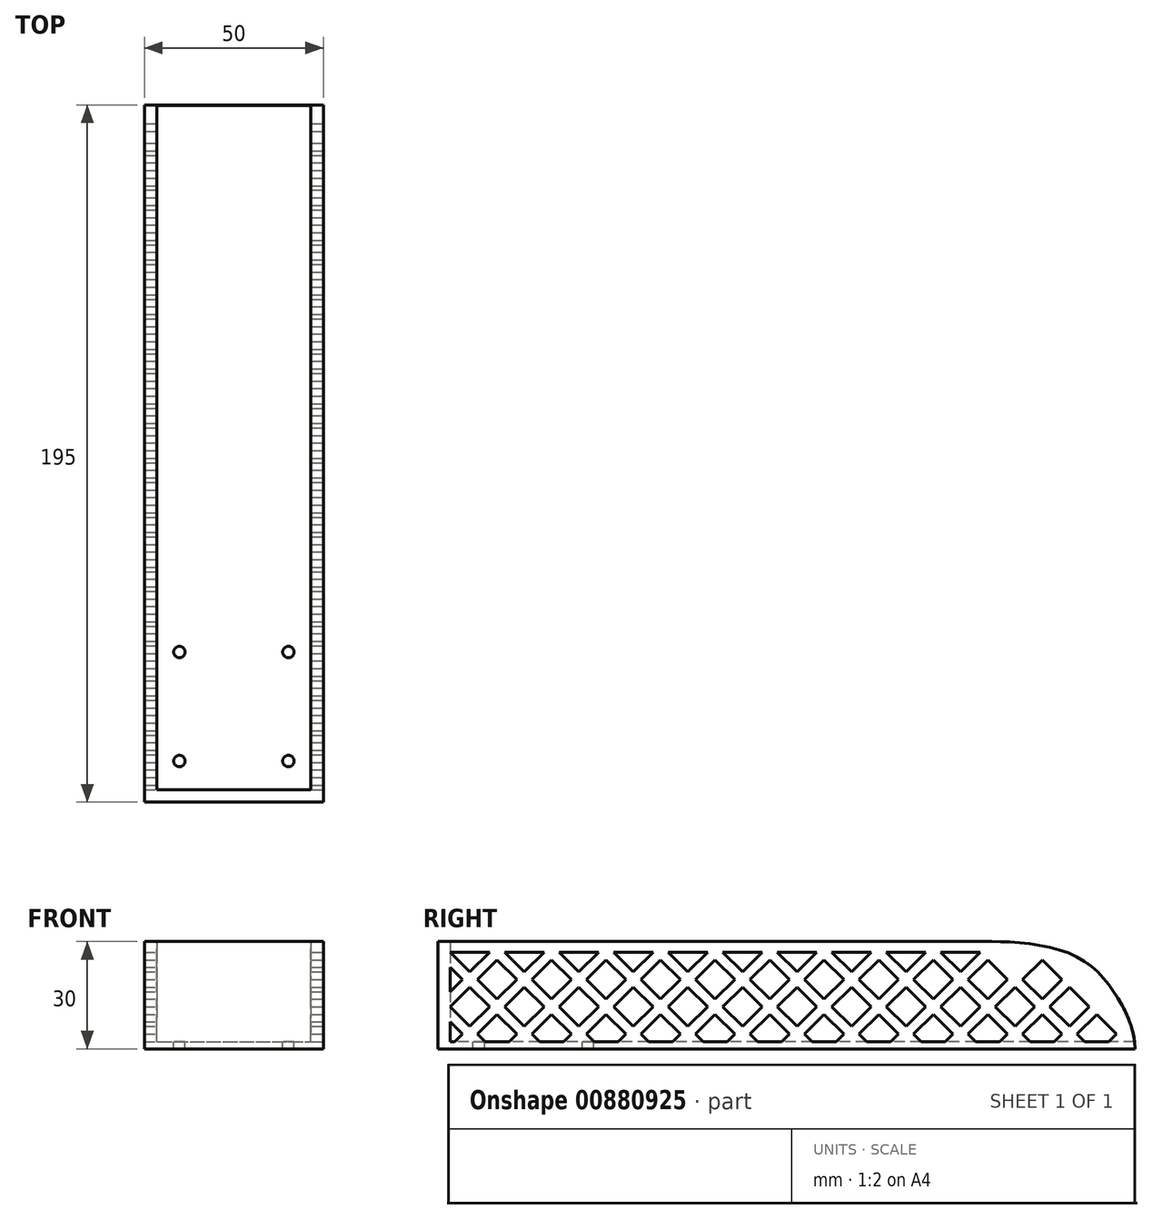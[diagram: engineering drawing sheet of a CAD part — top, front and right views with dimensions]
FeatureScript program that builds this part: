
annotation { "Feature Type Name" : "Feature", "Feature Type Description" : "" }
export const myFeature = defineFeature(function(context is Context, id is Id, definition is map)
    precondition{}
    {
        {
            var Q0;
            Q0=qCreatedBy(makeId("Top.planeOp"),FACE);
            var sketch = newSketch(context, id + "F0", { "sketchPlane" : qUnion([Q0])});
            skLineSegment(sketch, "E0.bottom", {"start": v(0, 0) * mm, "end": v(50, 0) * mm});
            skLineSegment(sketch, "E0.top", {"start": v(0, 195) * mm, "end": v(50, 195) * mm});
            skLineSegment(sketch, "E0.left", {"start": v(0, 0) * mm, "end": v(0, 195) * mm});
            skLineSegment(sketch, "E0.right", {"start": v(50, 0) * mm, "end": v(50, 195) * mm});
            skSolve(sketch);
        }
        {
            var Q0;
            Q0=makeQuery(id+"F0.imprint","IMPRINT",FACE,{"disambiguationData":[TD([[makeQuery(id+"F0.imprint","IMPRINT",EDGE,{"derivedFrom":sQuery(id+"F0.wireOp",EDGE,"E0.bottom")}),1.0]])]});
            extrude(context, id + "F1", {"entities" : qUnion([Q0]), "depth" : 2 * mm, "offsetDistance" : 25 * mm});
        }
        {
            var Q0;
            Q0=makeQuery(id+"F1.opExtrude","CAP_FACE",FACE,{"disambiguationData":[OSD([sQuery(id+"F0.wireOp",EDGE,"E0.bottom"),sQuery(id+"F0.wireOp",EDGE,"E0.top"),sQuery(id+"F0.wireOp",EDGE,"E0.left"),sQuery(id+"F0.wireOp",EDGE,"E0.right")])],"isStart":false});
            var sketch = newSketch(context, id + "F2", { "sketchPlane" : qUnion([Q0])});
            skLineSegment(sketch, "E1.0.0", {"start": v(50, 195) * mm, "end": v(0, 195) * mm});
            skLineSegment(sketch, "E1.0.1", {"start": v(0, 195) * mm, "end": v(0, 0) * mm});
            skLineSegment(sketch, "E1.0.2", {"start": v(0, 0) * mm, "end": v(50, 0) * mm});
            skLineSegment(sketch, "E1.0.3", {"start": v(50, 0) * mm, "end": v(50, 195) * mm});
            skLineSegment(sketch, "E2", {"start": v(3.5, 195) * mm, "end": v(3.5, 3.5) * mm});
            skLineSegment(sketch, "E3", {"start": v(3.5, 3.5) * mm, "end": v(46.5, 3.5) * mm});
            skLineSegment(sketch, "E4", {"start": v(46.5, 3.5) * mm, "end": v(46.5, 195) * mm});
            skLineSegment(sketch, "E5", {"start": v(0, 195) * mm, "end": v(3.5, 195) * mm});
            skLineSegment(sketch, "E6", {"start": v(46.5, 195) * mm, "end": v(50, 195) * mm});
            skSolve(sketch);
        }
        {
            var Q0;
            {var subQ0=sQuery(id+"F2.wireOp",EDGE,"E1.0.1");Q0=makeQuery(id+"F2.imprint","IMPRINT",FACE,{"disambiguationData":[TD([[makeQuery(id+"F2.imprint","IMPRINT",EDGE,{"derivedFrom":subQ0}),-1.0]])]});}
            extrude(context, id + "F3", {"entities" : qUnion([Q0]), "operationType" : NewBodyOperationType.ADD, "depth" : 28 * mm, "offsetDistance" : 25 * mm});
        }
        {
            var Q0;
            Q0=makeQuery(id+"F3.boolean.opBoolean","MERGE",FACE,{"derivedFrom":[makeQuery(id+"F1.opExtrude","SWEPT_FACE",FACE,{"disambiguationData":[OSD([sQuery(id+"F0.wireOp",EDGE,"E0.right")])]}),makeQuery(id+"F3.opExtrude","SWEPT_FACE",FACE,{"disambiguationData":[OSD([sQuery(id+"F2.wireOp",EDGE,"E1.0.3")])]})]});
            var sketch = newSketch(context, id + "F4", { "sketchPlane" : qUnion([Q0])});
            skLineSegment(sketch, "E7.0.0", {"start": v(0, 0) * mm, "end": v(195, 0) * mm});
            skLineSegment(sketch, "E7.0.1", {"start": v(195, 0) * mm, "end": v(195, 30) * mm});
            skLineSegment(sketch, "E7.0.2", {"start": v(195, 30) * mm, "end": v(0, 30) * mm});
            skLineSegment(sketch, "E7.0.3", {"start": v(0, 30) * mm, "end": v(0, 0) * mm});
            skFitSpline(sketch, "E8", {"points": [v(195, 0) * mm, v(190.35, 13.95) * mm, v(177.8, 26.18) * mm, v(155, 30) * mm], "startDerivative": vector(0, 46.4) * mm, "endDerivative": vector(-53.38, 0) * mm});
            skSolve(sketch);
        }
        {
            var Q0;
            {var subQ0=sQuery(id+"F4.wireOp",EDGE,"E7.0.1");Q0=makeQuery(id+"F4.imprint","IMPRINT",FACE,{"disambiguationData":[TD([[makeQuery(id+"F4.imprint","IMPRINT",EDGE,{"derivedFrom":subQ0}),-1.0]])]});}
            extrude(context, id + "F5", {"entities" : qUnion([Q0]), "operationType" : NewBodyOperationType.REMOVE, "endBound" : BoundingType.THROUGH_ALL, "oppositeDirection" : true, "depth" : 25 * mm, "offsetDistance" : 25 * mm});
        }
        {
            var Q0;
            Q0=makeQuery(id+"F3.boolean.opBoolean","MERGE",FACE,{"derivedFrom":[makeQuery(id+"F1.opExtrude","SWEPT_FACE",FACE,{"disambiguationData":[OSD([sQuery(id+"F0.wireOp",EDGE,"E0.right")])]}),makeQuery(id+"F3.opExtrude","SWEPT_FACE",FACE,{"disambiguationData":[OSD([sQuery(id+"F2.wireOp",EDGE,"E1.0.3")])]})]});
            var sketch = newSketch(context, id + "F6", { "sketchPlane" : qUnion([Q0])});
            skLineSegment(sketch, "E9.0.0", {"start": v(0, 0) * mm, "end": v(195, 0) * mm});
            skFitSpline(sketch, "E9.0.1", {"points": [v(195, 0) * mm, v(195, 4.62) * mm, v(190.89, 14.7) * mm, v(179.29, 28.71) * mm, v(161.67, 30) * mm, v(155, 30) * mm]});
            skLineSegment(sketch, "E9.0.2", {"start": v(155, 30) * mm, "end": v(0, 30) * mm});
            skLineSegment(sketch, "E9.0.3", {"start": v(0, 30) * mm, "end": v(0, 0) * mm});
            skLineSegment(sketch, "E10.0.1", {"start": v(3.5, 2) * mm, "end": v(3.5, 30) * mm});
            skLineSegment(sketch, "E10.0.3", {"start": v(3.5, 30) * mm, "end": v(3.5, 2) * mm});
            skLineSegment(sketch, "E11.0.0", {"start": v(3.5, 2) * mm, "end": v(194.88, 2) * mm});
            skLineSegment(sketch, "E11.0.2", {"start": v(194.88, 2) * mm, "end": v(3.5, 2) * mm});
            skLineSegment(sketch, "E12.0", {"start": v(155, 27) * mm, "end": v(0, 27) * mm});
            skFitSpline(sketch, "E12.1", {"points": [v(192, 0) * mm, v(192, 0.79) * mm, v(191.86, 2.41) * mm, v(191.25, 4.98) * mm, v(190.28, 7.63) * mm, v(189.2, 9.87) * mm, v(188.22, 11.66) * mm, v(187.16, 13.45) * mm, v(185.75, 15.6) * mm, v(183.86, 17.98) * mm, v(181.74, 20.11) * mm, v(179.74, 21.66) * mm, v(177.97, 22.74) * mm, v(176.56, 23.47) * mm, v(175.02, 24.12) * mm, v(173.36, 24.7) * mm, v(171.6, 25.2) * mm, v(169.17, 25.78) * mm, v(165.98, 26.33) * mm, v(160.83, 26.89) * mm, v(157.16, 27) * mm, v(155, 27) * mm]});
            skLineSegment(sketch, "E13", {"start": v(3.5, 27) * mm, "end": v(9, 21.5) * mm});
            skLineSegment(sketch, "E14", {"start": v(9, 21.5) * mm, "end": v(14.5, 27) * mm});
            skLineSegment(sketch, "E15", {"start": v(3.5, 22.76) * mm, "end": v(6.88, 19.38) * mm});
            skLineSegment(sketch, "E16", {"start": v(6.88, 19.38) * mm, "end": v(3.5, 16) * mm});
            skLineSegment(sketch, "E17", {"start": v(9, 17.26) * mm, "end": v(3.5, 11.76) * mm});
            skLineSegment(sketch, "E18", {"start": v(3.5, 11.76) * mm, "end": v(9, 6.26) * mm});
            skLineSegment(sketch, "E19", {"start": v(9, 6.26) * mm, "end": v(14.5, 11.76) * mm});
            skLineSegment(sketch, "E20", {"start": v(14.5, 11.76) * mm, "end": v(9, 17.26) * mm});
            skLineSegment(sketch, "E21", {"start": v(6.88, 19.38) * mm, "end": v(9, 21.5) * mm, "construction": true});
            skLineSegment(sketch, "E22", {"start": v(3.5, 11.76) * mm, "end": v(14.5, 11.76) * mm, "construction": true});
            skLineSegment(sketch, "E23.MirrorCS", {"start": v(4.74, 2) * mm, "end": v(6.88, 4.14) * mm});
            skLineSegment(sketch, "E24.MirrorCS", {"start": v(6.88, 4.14) * mm, "end": v(3.5, 7.51) * mm});
            skPoint(sketch, "E25.orphan", {"position": v(3.5, 0.76) * mm});
            skLineSegment(sketch, "E26", {"start": v(9, 21.5) * mm, "end": v(9, 17.26) * mm, "construction": true});
            skLineSegment(sketch, "E27", {"start": v(11.12, 19.38) * mm, "end": v(16.62, 24.88) * mm});
            skLineSegment(sketch, "E28", {"start": v(11.12, 19.38) * mm, "end": v(16.62, 13.88) * mm});
            skLineSegment(sketch, "E29", {"start": v(16.62, 13.88) * mm, "end": v(22.12, 19.38) * mm});
            skLineSegment(sketch, "E30", {"start": v(22.12, 19.38) * mm, "end": v(16.62, 24.88) * mm});
            skLineSegment(sketch, "E31", {"start": v(6.88, 19.38) * mm, "end": v(11.12, 19.38) * mm, "construction": true});
            skLineSegment(sketch, "E32.MirrorCS", {"start": v(11.12, 4.14) * mm, "end": v(13.26, 2) * mm});
            skLineSegment(sketch, "E33.MirrorCS", {"start": v(22.12, 4.14) * mm, "end": v(19.99, 2) * mm});
            skLineSegment(sketch, "E34.MirrorCS", {"start": v(16.62, 9.64) * mm, "end": v(22.12, 4.14) * mm});
            skLineSegment(sketch, "E35.MirrorCS", {"start": v(11.12, 4.14) * mm, "end": v(16.62, 9.64) * mm});
            skPoint(sketch, "E36.orphan", {"position": v(16.62, -1.36) * mm});
            skLineSegment(sketch, "E37.1.0.0", {"start": v(18.74, 27) * mm, "end": v(24.24, 21.5) * mm});
            skLineSegment(sketch, "E37.1.0.1", {"start": v(24.24, 21.5) * mm, "end": v(29.74, 27) * mm});
            skLineSegment(sketch, "E37.1.0.2", {"start": v(26.36, 19.38) * mm, "end": v(31.86, 24.88) * mm});
            skLineSegment(sketch, "E37.1.0.3", {"start": v(37.36, 19.38) * mm, "end": v(31.86, 24.88) * mm});
            skLineSegment(sketch, "E37.1.0.4", {"start": v(31.86, 13.88) * mm, "end": v(37.36, 19.38) * mm});
            skLineSegment(sketch, "E37.1.0.5", {"start": v(26.36, 19.38) * mm, "end": v(31.86, 13.88) * mm});
            skLineSegment(sketch, "E37.1.0.6", {"start": v(29.74, 11.76) * mm, "end": v(24.24, 17.26) * mm});
            skLineSegment(sketch, "E37.1.0.7", {"start": v(24.24, 17.26) * mm, "end": v(18.74, 11.76) * mm});
            skLineSegment(sketch, "E37.1.0.8", {"start": v(18.74, 11.76) * mm, "end": v(24.24, 6.26) * mm});
            skLineSegment(sketch, "E37.1.0.9", {"start": v(24.24, 6.26) * mm, "end": v(29.74, 11.76) * mm});
            skLineSegment(sketch, "E37.1.0.10", {"start": v(26.36, 4.14) * mm, "end": v(31.86, 9.64) * mm});
            skLineSegment(sketch, "E37.1.0.11", {"start": v(31.86, 9.64) * mm, "end": v(37.36, 4.14) * mm});
            skLineSegment(sketch, "E37.1.0.12", {"start": v(37.36, 4.14) * mm, "end": v(35.23, 2) * mm});
            skLineSegment(sketch, "E37.1.0.13", {"start": v(26.36, 4.14) * mm, "end": v(28.5, 2) * mm});
            skLineSegment(sketch, "E37.2.0.0", {"start": v(33.99, 27) * mm, "end": v(39.49, 21.5) * mm});
            skLineSegment(sketch, "E37.2.0.1", {"start": v(39.49, 21.5) * mm, "end": v(44.99, 27) * mm});
            skLineSegment(sketch, "E37.2.0.2", {"start": v(41.6, 19.38) * mm, "end": v(47.1, 24.88) * mm});
            skLineSegment(sketch, "E37.2.0.3", {"start": v(52.6, 19.38) * mm, "end": v(47.1, 24.88) * mm});
            skLineSegment(sketch, "E37.2.0.4", {"start": v(47.1, 13.88) * mm, "end": v(52.6, 19.38) * mm});
            skLineSegment(sketch, "E37.2.0.5", {"start": v(41.6, 19.38) * mm, "end": v(47.1, 13.88) * mm});
            skLineSegment(sketch, "E37.2.0.6", {"start": v(44.99, 11.76) * mm, "end": v(39.49, 17.26) * mm});
            skLineSegment(sketch, "E37.2.0.7", {"start": v(39.49, 17.26) * mm, "end": v(33.99, 11.76) * mm});
            skLineSegment(sketch, "E37.2.0.8", {"start": v(33.99, 11.76) * mm, "end": v(39.49, 6.26) * mm});
            skLineSegment(sketch, "E37.2.0.9", {"start": v(39.49, 6.26) * mm, "end": v(44.99, 11.76) * mm});
            skLineSegment(sketch, "E37.2.0.10", {"start": v(41.6, 4.14) * mm, "end": v(47.1, 9.64) * mm});
            skLineSegment(sketch, "E37.2.0.11", {"start": v(47.1, 9.64) * mm, "end": v(52.6, 4.14) * mm});
            skLineSegment(sketch, "E37.2.0.12", {"start": v(52.6, 4.14) * mm, "end": v(50.47, 2) * mm});
            skLineSegment(sketch, "E37.2.0.13", {"start": v(41.6, 4.14) * mm, "end": v(43.74, 2) * mm});
            skLineSegment(sketch, "E37.3.0.0", {"start": v(49.23, 27) * mm, "end": v(54.73, 21.5) * mm});
            skLineSegment(sketch, "E37.3.0.1", {"start": v(54.73, 21.5) * mm, "end": v(60.23, 27) * mm});
            skLineSegment(sketch, "E37.3.0.2", {"start": v(56.85, 19.38) * mm, "end": v(62.35, 24.88) * mm});
            skLineSegment(sketch, "E37.3.0.3", {"start": v(67.85, 19.38) * mm, "end": v(62.35, 24.88) * mm});
            skLineSegment(sketch, "E37.3.0.4", {"start": v(62.35, 13.88) * mm, "end": v(67.85, 19.38) * mm});
            skLineSegment(sketch, "E37.3.0.5", {"start": v(56.85, 19.38) * mm, "end": v(62.35, 13.88) * mm});
            skLineSegment(sketch, "E37.3.0.6", {"start": v(60.23, 11.76) * mm, "end": v(54.73, 17.26) * mm});
            skLineSegment(sketch, "E37.3.0.7", {"start": v(54.73, 17.26) * mm, "end": v(49.23, 11.76) * mm});
            skLineSegment(sketch, "E37.3.0.8", {"start": v(49.23, 11.76) * mm, "end": v(54.73, 6.26) * mm});
            skLineSegment(sketch, "E37.3.0.9", {"start": v(54.73, 6.26) * mm, "end": v(60.23, 11.76) * mm});
            skLineSegment(sketch, "E37.3.0.10", {"start": v(56.85, 4.14) * mm, "end": v(62.35, 9.64) * mm});
            skLineSegment(sketch, "E37.3.0.11", {"start": v(62.35, 9.64) * mm, "end": v(67.85, 4.14) * mm});
            skLineSegment(sketch, "E37.3.0.12", {"start": v(67.85, 4.14) * mm, "end": v(65.71, 2) * mm});
            skLineSegment(sketch, "E37.3.0.13", {"start": v(56.85, 4.14) * mm, "end": v(58.99, 2) * mm});
            skLineSegment(sketch, "E37.4.0.0", {"start": v(64.47, 27) * mm, "end": v(69.97, 21.5) * mm});
            skLineSegment(sketch, "E37.4.0.1", {"start": v(69.97, 21.5) * mm, "end": v(75.47, 27) * mm});
            skLineSegment(sketch, "E37.4.0.2", {"start": v(72.1, 19.38) * mm, "end": v(77.6, 24.88) * mm});
            skLineSegment(sketch, "E37.4.0.3", {"start": v(83.1, 19.38) * mm, "end": v(77.6, 24.88) * mm});
            skLineSegment(sketch, "E37.4.0.4", {"start": v(77.6, 13.88) * mm, "end": v(83.1, 19.38) * mm});
            skLineSegment(sketch, "E37.4.0.5", {"start": v(72.1, 19.38) * mm, "end": v(77.6, 13.88) * mm});
            skLineSegment(sketch, "E37.4.0.6", {"start": v(75.47, 11.76) * mm, "end": v(69.97, 17.26) * mm});
            skLineSegment(sketch, "E37.4.0.7", {"start": v(69.97, 17.26) * mm, "end": v(64.47, 11.76) * mm});
            skLineSegment(sketch, "E37.4.0.8", {"start": v(64.47, 11.76) * mm, "end": v(69.97, 6.26) * mm});
            skLineSegment(sketch, "E37.4.0.9", {"start": v(69.97, 6.26) * mm, "end": v(75.47, 11.76) * mm});
            skLineSegment(sketch, "E37.4.0.10", {"start": v(72.1, 4.14) * mm, "end": v(77.6, 9.64) * mm});
            skLineSegment(sketch, "E37.4.0.11", {"start": v(77.6, 9.64) * mm, "end": v(83.1, 4.14) * mm});
            skLineSegment(sketch, "E37.4.0.12", {"start": v(83.1, 4.14) * mm, "end": v(80.96, 2) * mm});
            skLineSegment(sketch, "E37.4.0.13", {"start": v(72.1, 4.14) * mm, "end": v(74.23, 2) * mm});
            skLineSegment(sketch, "E37.5.0.0", {"start": v(79.72, 27) * mm, "end": v(85.22, 21.5) * mm});
            skLineSegment(sketch, "E37.5.0.1", {"start": v(85.22, 21.5) * mm, "end": v(90.72, 27) * mm});
            skLineSegment(sketch, "E37.5.0.2", {"start": v(87.34, 19.38) * mm, "end": v(92.84, 24.88) * mm});
            skLineSegment(sketch, "E37.5.0.3", {"start": v(98.34, 19.38) * mm, "end": v(92.84, 24.88) * mm});
            skLineSegment(sketch, "E37.5.0.4", {"start": v(92.84, 13.88) * mm, "end": v(98.34, 19.38) * mm});
            skLineSegment(sketch, "E37.5.0.5", {"start": v(87.34, 19.38) * mm, "end": v(92.84, 13.88) * mm});
            skLineSegment(sketch, "E37.5.0.6", {"start": v(90.72, 11.76) * mm, "end": v(85.22, 17.26) * mm});
            skLineSegment(sketch, "E37.5.0.7", {"start": v(85.22, 17.26) * mm, "end": v(79.72, 11.76) * mm});
            skLineSegment(sketch, "E37.5.0.8", {"start": v(79.72, 11.76) * mm, "end": v(85.22, 6.26) * mm});
            skLineSegment(sketch, "E37.5.0.9", {"start": v(85.22, 6.26) * mm, "end": v(90.72, 11.76) * mm});
            skLineSegment(sketch, "E37.5.0.10", {"start": v(87.34, 4.14) * mm, "end": v(92.84, 9.64) * mm});
            skLineSegment(sketch, "E37.5.0.11", {"start": v(92.84, 9.64) * mm, "end": v(98.34, 4.14) * mm});
            skLineSegment(sketch, "E37.5.0.12", {"start": v(98.34, 4.14) * mm, "end": v(96.2, 2) * mm});
            skLineSegment(sketch, "E37.5.0.13", {"start": v(87.34, 4.14) * mm, "end": v(89.47, 2) * mm});
            skLineSegment(sketch, "E37.6.0.0", {"start": v(94.96, 27) * mm, "end": v(100.46, 21.5) * mm});
            skLineSegment(sketch, "E37.6.0.1", {"start": v(100.46, 21.5) * mm, "end": v(105.96, 27) * mm});
            skLineSegment(sketch, "E37.6.0.2", {"start": v(102.58, 19.38) * mm, "end": v(108.08, 24.88) * mm});
            skLineSegment(sketch, "E37.6.0.3", {"start": v(113.58, 19.38) * mm, "end": v(108.08, 24.88) * mm});
            skLineSegment(sketch, "E37.6.0.4", {"start": v(108.08, 13.88) * mm, "end": v(113.58, 19.38) * mm});
            skLineSegment(sketch, "E37.6.0.5", {"start": v(102.58, 19.38) * mm, "end": v(108.08, 13.88) * mm});
            skLineSegment(sketch, "E37.6.0.6", {"start": v(105.96, 11.76) * mm, "end": v(100.46, 17.26) * mm});
            skLineSegment(sketch, "E37.6.0.7", {"start": v(100.46, 17.26) * mm, "end": v(94.96, 11.76) * mm});
            skLineSegment(sketch, "E37.6.0.8", {"start": v(94.96, 11.76) * mm, "end": v(100.46, 6.26) * mm});
            skLineSegment(sketch, "E37.6.0.9", {"start": v(100.46, 6.26) * mm, "end": v(105.96, 11.76) * mm});
            skLineSegment(sketch, "E37.6.0.10", {"start": v(102.58, 4.14) * mm, "end": v(108.08, 9.64) * mm});
            skLineSegment(sketch, "E37.6.0.11", {"start": v(108.08, 9.64) * mm, "end": v(113.58, 4.14) * mm});
            skLineSegment(sketch, "E37.6.0.12", {"start": v(113.58, 4.14) * mm, "end": v(111.44, 2) * mm});
            skLineSegment(sketch, "E37.6.0.13", {"start": v(102.58, 4.14) * mm, "end": v(104.72, 2) * mm});
            skLineSegment(sketch, "E37.7.0.0", {"start": v(110.2, 27) * mm, "end": v(115.7, 21.5) * mm});
            skLineSegment(sketch, "E37.7.0.1", {"start": v(115.7, 21.5) * mm, "end": v(121.2, 27) * mm});
            skLineSegment(sketch, "E37.7.0.2", {"start": v(117.82, 19.38) * mm, "end": v(123.32, 24.88) * mm});
            skLineSegment(sketch, "E37.7.0.3", {"start": v(128.82, 19.38) * mm, "end": v(123.32, 24.88) * mm});
            skLineSegment(sketch, "E37.7.0.4", {"start": v(123.32, 13.88) * mm, "end": v(128.82, 19.38) * mm});
            skLineSegment(sketch, "E37.7.0.5", {"start": v(117.82, 19.38) * mm, "end": v(123.32, 13.88) * mm});
            skLineSegment(sketch, "E37.7.0.6", {"start": v(121.2, 11.76) * mm, "end": v(115.7, 17.26) * mm});
            skLineSegment(sketch, "E37.7.0.7", {"start": v(115.7, 17.26) * mm, "end": v(110.2, 11.76) * mm});
            skLineSegment(sketch, "E37.7.0.8", {"start": v(110.2, 11.76) * mm, "end": v(115.7, 6.26) * mm});
            skLineSegment(sketch, "E37.7.0.9", {"start": v(115.7, 6.26) * mm, "end": v(121.2, 11.76) * mm});
            skLineSegment(sketch, "E37.7.0.10", {"start": v(117.82, 4.14) * mm, "end": v(123.32, 9.64) * mm});
            skLineSegment(sketch, "E37.7.0.11", {"start": v(123.32, 9.64) * mm, "end": v(128.82, 4.14) * mm});
            skLineSegment(sketch, "E37.7.0.12", {"start": v(128.82, 4.14) * mm, "end": v(126.69, 2) * mm});
            skLineSegment(sketch, "E37.7.0.13", {"start": v(117.82, 4.14) * mm, "end": v(119.96, 2) * mm});
            skLineSegment(sketch, "E37.8.0.0", {"start": v(125.44, 27) * mm, "end": v(130.94, 21.5) * mm});
            skLineSegment(sketch, "E37.8.0.1", {"start": v(130.94, 21.5) * mm, "end": v(136.44, 27) * mm});
            skLineSegment(sketch, "E37.8.0.2", {"start": v(133.07, 19.38) * mm, "end": v(138.57, 24.88) * mm});
            skLineSegment(sketch, "E37.8.0.3", {"start": v(144.07, 19.38) * mm, "end": v(138.57, 24.88) * mm});
            skLineSegment(sketch, "E37.8.0.4", {"start": v(138.57, 13.88) * mm, "end": v(144.07, 19.38) * mm});
            skLineSegment(sketch, "E37.8.0.5", {"start": v(133.07, 19.38) * mm, "end": v(138.57, 13.88) * mm});
            skLineSegment(sketch, "E37.8.0.6", {"start": v(136.44, 11.76) * mm, "end": v(130.94, 17.26) * mm});
            skLineSegment(sketch, "E37.8.0.7", {"start": v(130.94, 17.26) * mm, "end": v(125.44, 11.76) * mm});
            skLineSegment(sketch, "E37.8.0.8", {"start": v(125.44, 11.76) * mm, "end": v(130.94, 6.26) * mm});
            skLineSegment(sketch, "E37.8.0.9", {"start": v(130.94, 6.26) * mm, "end": v(136.44, 11.76) * mm});
            skLineSegment(sketch, "E37.8.0.10", {"start": v(133.07, 4.14) * mm, "end": v(138.57, 9.64) * mm});
            skLineSegment(sketch, "E37.8.0.11", {"start": v(138.57, 9.64) * mm, "end": v(144.07, 4.14) * mm});
            skLineSegment(sketch, "E37.8.0.12", {"start": v(144.07, 4.14) * mm, "end": v(141.93, 2) * mm});
            skLineSegment(sketch, "E37.8.0.13", {"start": v(133.07, 4.14) * mm, "end": v(135.2, 2) * mm});
            skLineSegment(sketch, "E37.9.0.0", {"start": v(140.69, 27) * mm, "end": v(146.19, 21.5) * mm});
            skLineSegment(sketch, "E37.9.0.1", {"start": v(146.19, 21.5) * mm, "end": v(151.69, 27) * mm});
            skLineSegment(sketch, "E37.9.0.2", {"start": v(148.3, 19.38) * mm, "end": v(153.8, 24.88) * mm});
            skLineSegment(sketch, "E37.9.0.3", {"start": v(159.3, 19.38) * mm, "end": v(153.8, 24.88) * mm});
            skLineSegment(sketch, "E37.9.0.4", {"start": v(153.8, 13.88) * mm, "end": v(159.3, 19.38) * mm});
            skLineSegment(sketch, "E37.9.0.5", {"start": v(148.3, 19.38) * mm, "end": v(153.8, 13.88) * mm});
            skLineSegment(sketch, "E37.9.0.6", {"start": v(151.69, 11.76) * mm, "end": v(146.19, 17.26) * mm});
            skLineSegment(sketch, "E37.9.0.7", {"start": v(146.19, 17.26) * mm, "end": v(140.69, 11.76) * mm});
            skLineSegment(sketch, "E37.9.0.8", {"start": v(140.69, 11.76) * mm, "end": v(146.19, 6.26) * mm});
            skLineSegment(sketch, "E37.9.0.9", {"start": v(146.19, 6.26) * mm, "end": v(151.69, 11.76) * mm});
            skLineSegment(sketch, "E37.9.0.10", {"start": v(148.3, 4.14) * mm, "end": v(153.8, 9.64) * mm});
            skLineSegment(sketch, "E37.9.0.11", {"start": v(153.8, 9.64) * mm, "end": v(159.3, 4.14) * mm});
            skLineSegment(sketch, "E37.9.0.12", {"start": v(159.3, 4.14) * mm, "end": v(157.17, 2) * mm});
            skLineSegment(sketch, "E37.9.0.13", {"start": v(148.3, 4.14) * mm, "end": v(150.44, 2) * mm});
            skLineSegment(sketch, "E37.10.0.0", {"start": v(155.93, 27) * mm, "end": v(161.43, 21.5) * mm});
            skLineSegment(sketch, "E37.10.0.1", {"start": v(161.43, 21.5) * mm, "end": v(166.2, 26.26) * mm});
            skLineSegment(sketch, "E37.10.0.2", {"start": v(163.55, 19.38) * mm, "end": v(169.05, 24.88) * mm});
            skLineSegment(sketch, "E37.10.0.3", {"start": v(174.55, 19.38) * mm, "end": v(169.05, 24.88) * mm});
            skLineSegment(sketch, "E37.10.0.4", {"start": v(169.05, 13.88) * mm, "end": v(174.55, 19.38) * mm});
            skLineSegment(sketch, "E37.10.0.5", {"start": v(163.55, 19.38) * mm, "end": v(169.05, 13.88) * mm});
            skLineSegment(sketch, "E37.10.0.6", {"start": v(166.93, 11.76) * mm, "end": v(161.43, 17.26) * mm});
            skLineSegment(sketch, "E37.10.0.7", {"start": v(161.43, 17.26) * mm, "end": v(155.93, 11.76) * mm});
            skLineSegment(sketch, "E37.10.0.8", {"start": v(155.93, 11.76) * mm, "end": v(161.43, 6.26) * mm});
            skLineSegment(sketch, "E37.10.0.9", {"start": v(161.43, 6.26) * mm, "end": v(166.93, 11.76) * mm});
            skLineSegment(sketch, "E37.10.0.10", {"start": v(163.55, 4.14) * mm, "end": v(169.05, 9.64) * mm});
            skLineSegment(sketch, "E37.10.0.11", {"start": v(169.05, 9.64) * mm, "end": v(174.55, 4.14) * mm});
            skLineSegment(sketch, "E37.10.0.12", {"start": v(174.55, 4.14) * mm, "end": v(172.42, 2) * mm});
            skLineSegment(sketch, "E37.10.0.13", {"start": v(163.55, 4.14) * mm, "end": v(165.69, 2) * mm});
            skLineSegment(sketch, "E37.11.0.0", {"start": v(173.55, 24.62) * mm, "end": v(176.67, 21.5) * mm});
            skLineSegment(sketch, "E37.11.0.1", {"start": v(176.67, 21.5) * mm, "end": v(177.92, 22.75) * mm});
            skLineSegment(sketch, "E37.11.0.2", {"start": v(178.8, 19.38) * mm, "end": v(180.48, 21.06) * mm});
            skLineSegment(sketch, "E37.11.0.4", {"start": v(184.3, 13.88) * mm, "end": v(185.83, 15.41) * mm});
            skLineSegment(sketch, "E37.11.0.5", {"start": v(178.8, 19.38) * mm, "end": v(184.3, 13.88) * mm});
            skLineSegment(sketch, "E37.11.0.6", {"start": v(182.17, 11.76) * mm, "end": v(176.67, 17.26) * mm});
            skLineSegment(sketch, "E37.11.0.7", {"start": v(176.67, 17.26) * mm, "end": v(171.17, 11.76) * mm});
            skLineSegment(sketch, "E37.11.0.8", {"start": v(171.17, 11.76) * mm, "end": v(176.67, 6.26) * mm});
            skLineSegment(sketch, "E37.11.0.9", {"start": v(176.67, 6.26) * mm, "end": v(182.17, 11.76) * mm});
            skLineSegment(sketch, "E37.11.0.10", {"start": v(178.8, 4.14) * mm, "end": v(184.3, 9.64) * mm});
            skLineSegment(sketch, "E37.11.0.11", {"start": v(184.3, 9.64) * mm, "end": v(189.8, 4.14) * mm});
            skLineSegment(sketch, "E37.11.0.12", {"start": v(189.8, 4.14) * mm, "end": v(187.66, 2) * mm});
            skLineSegment(sketch, "E37.11.0.13", {"start": v(178.8, 4.14) * mm, "end": v(180.93, 2) * mm});
            skLineSegment(sketch, "E37.direction1", {"start": v(9, 21.5) * mm, "end": v(24.24, 21.5) * mm, "construction": true});
            skPoint(sketch, "E38.orphan", {"position": v(166.93, 27) * mm});
            skPoint(sketch, "E39.orphan", {"position": v(171.17, 27) * mm});
            skPoint(sketch, "E40.orphan", {"position": v(182.17, 27) * mm});
            skPoint(sketch, "E41.orphan", {"position": v(184.3, 24.88) * mm});
            skPoint(sketch, "E42.orphan", {"position": v(189.8, 19.38) * mm});
            skSolve(sketch);
        }
        {
            var Q0;
            {var subQ0=sQuery(id+"F6.wireOp",EDGE,"E13");Q0=makeQuery(id+"F6.imprint","IMPRINT",FACE,{"disambiguationData":[TD([[makeQuery(id+"F6.imprint","IMPRINT",EDGE,{"derivedFrom":subQ0}),1.0]])]});}
            var Q1;
            {var subQ0=sQuery(id+"F6.wireOp",EDGE,"E15");Q1=makeQuery(id+"F6.imprint","IMPRINT",FACE,{"disambiguationData":[TD([[makeQuery(id+"F6.imprint","IMPRINT",EDGE,{"derivedFrom":subQ0}),-1.0]])]});}
            var Q2;
            Q2=makeQuery(id+"F6.imprint","IMPRINT",FACE,{"disambiguationData":[TD([[makeQuery(id+"F6.imprint","IMPRINT",EDGE,{"derivedFrom":sQuery(id+"F6.wireOp",EDGE,"E17")}),1.0]])]});
            var Q3;
            {var subQ4=sQuery(id+"F6.wireOp",EDGE,"E23.MirrorCS");Q3=makeQuery(id+"F6.imprint","IMPRINT",FACE,{"disambiguationData":[TD([[makeQuery(id+"F6.imprint","IMPRINT",EDGE,{"derivedFrom":subQ4}),1.0]])]});}
            var Q4;
            {var subQ1=sQuery(id+"F6.wireOp",EDGE,"E32.MirrorCS");Q4=makeQuery(id+"F6.imprint","IMPRINT",FACE,{"disambiguationData":[TD([[makeQuery(id+"F6.imprint","IMPRINT",EDGE,{"derivedFrom":subQ1}),1.0]])]});}
            var Q5;
            Q5=makeQuery(id+"F6.imprint","IMPRINT",FACE,{"disambiguationData":[TD([[makeQuery(id+"F6.imprint","IMPRINT",EDGE,{"derivedFrom":sQuery(id+"F6.wireOp",EDGE,"E27")}),-1.0]])]});
            var Q6;
            {var subQ0=sQuery(id+"F6.wireOp",EDGE,"E37.1.0.0");Q6=makeQuery(id+"F6.imprint","IMPRINT",FACE,{"disambiguationData":[TD([[makeQuery(id+"F6.imprint","IMPRINT",EDGE,{"derivedFrom":subQ0}),1.0]])]});}
            var Q7;
            Q7=makeQuery(id+"F6.imprint","IMPRINT",FACE,{"disambiguationData":[TD([[makeQuery(id+"F6.imprint","IMPRINT",EDGE,{"derivedFrom":sQuery(id+"F6.wireOp",EDGE,"E37.1.0.6")}),1.0]])]});
            var Q8;
            Q8=makeQuery(id+"F6.imprint","IMPRINT",FACE,{"disambiguationData":[TD([[makeQuery(id+"F6.imprint","IMPRINT",EDGE,{"derivedFrom":sQuery(id+"F6.wireOp",EDGE,"E37.1.0.2")}),-1.0]])]});
            var Q9;
            Q9=makeQuery(id+"F6.imprint","IMPRINT",FACE,{"disambiguationData":[TD([[makeQuery(id+"F6.imprint","IMPRINT",EDGE,{"derivedFrom":sQuery(id+"F6.wireOp",EDGE,"E37.1.0.10")}),-1.0]])]});
            var Q10;
            Q10=makeQuery(id+"F6.imprint","IMPRINT",FACE,{"disambiguationData":[TD([[makeQuery(id+"F6.imprint","IMPRINT",EDGE,{"derivedFrom":sQuery(id+"F6.wireOp",EDGE,"E37.2.0.6")}),1.0]])]});
            var Q11;
            {var subQ0=sQuery(id+"F6.wireOp",EDGE,"E37.2.0.0");Q11=makeQuery(id+"F6.imprint","IMPRINT",FACE,{"disambiguationData":[TD([[makeQuery(id+"F6.imprint","IMPRINT",EDGE,{"derivedFrom":subQ0}),1.0]])]});}
            var Q12;
            Q12=makeQuery(id+"F6.imprint","IMPRINT",FACE,{"disambiguationData":[TD([[makeQuery(id+"F6.imprint","IMPRINT",EDGE,{"derivedFrom":sQuery(id+"F6.wireOp",EDGE,"E37.2.0.2")}),-1.0]])]});
            var Q13;
            Q13=makeQuery(id+"F6.imprint","IMPRINT",FACE,{"disambiguationData":[TD([[makeQuery(id+"F6.imprint","IMPRINT",EDGE,{"derivedFrom":sQuery(id+"F6.wireOp",EDGE,"E37.2.0.10")}),-1.0]])]});
            var Q14;
            Q14=makeQuery(id+"F6.imprint","IMPRINT",FACE,{"disambiguationData":[TD([[makeQuery(id+"F6.imprint","IMPRINT",EDGE,{"derivedFrom":sQuery(id+"F6.wireOp",EDGE,"E37.3.0.6")}),1.0]])]});
            var Q15;
            {var subQ0=sQuery(id+"F6.wireOp",EDGE,"E37.3.0.0");Q15=makeQuery(id+"F6.imprint","IMPRINT",FACE,{"disambiguationData":[TD([[makeQuery(id+"F6.imprint","IMPRINT",EDGE,{"derivedFrom":subQ0}),1.0]])]});}
            var Q16;
            Q16=makeQuery(id+"F6.imprint","IMPRINT",FACE,{"disambiguationData":[TD([[makeQuery(id+"F6.imprint","IMPRINT",EDGE,{"derivedFrom":sQuery(id+"F6.wireOp",EDGE,"E37.3.0.2")}),-1.0]])]});
            var Q17;
            Q17=makeQuery(id+"F6.imprint","IMPRINT",FACE,{"disambiguationData":[TD([[makeQuery(id+"F6.imprint","IMPRINT",EDGE,{"derivedFrom":sQuery(id+"F6.wireOp",EDGE,"E37.3.0.10")}),-1.0]])]});
            var Q18;
            Q18=makeQuery(id+"F6.imprint","IMPRINT",FACE,{"disambiguationData":[TD([[makeQuery(id+"F6.imprint","IMPRINT",EDGE,{"derivedFrom":sQuery(id+"F6.wireOp",EDGE,"E37.4.0.6")}),1.0]])]});
            var Q19;
            {var subQ0=sQuery(id+"F6.wireOp",EDGE,"E37.4.0.0");Q19=makeQuery(id+"F6.imprint","IMPRINT",FACE,{"disambiguationData":[TD([[makeQuery(id+"F6.imprint","IMPRINT",EDGE,{"derivedFrom":subQ0}),1.0]])]});}
            var Q20;
            Q20=makeQuery(id+"F6.imprint","IMPRINT",FACE,{"disambiguationData":[TD([[makeQuery(id+"F6.imprint","IMPRINT",EDGE,{"derivedFrom":sQuery(id+"F6.wireOp",EDGE,"E37.4.0.2")}),-1.0]])]});
            var Q21;
            Q21=makeQuery(id+"F6.imprint","IMPRINT",FACE,{"disambiguationData":[TD([[makeQuery(id+"F6.imprint","IMPRINT",EDGE,{"derivedFrom":sQuery(id+"F6.wireOp",EDGE,"E37.4.0.10")}),-1.0]])]});
            var Q22;
            Q22=makeQuery(id+"F6.imprint","IMPRINT",FACE,{"disambiguationData":[TD([[makeQuery(id+"F6.imprint","IMPRINT",EDGE,{"derivedFrom":sQuery(id+"F6.wireOp",EDGE,"E37.5.0.6")}),1.0]])]});
            var Q23;
            {var subQ0=sQuery(id+"F6.wireOp",EDGE,"E37.5.0.0");Q23=makeQuery(id+"F6.imprint","IMPRINT",FACE,{"disambiguationData":[TD([[makeQuery(id+"F6.imprint","IMPRINT",EDGE,{"derivedFrom":subQ0}),1.0]])]});}
            var Q24;
            Q24=makeQuery(id+"F6.imprint","IMPRINT",FACE,{"disambiguationData":[TD([[makeQuery(id+"F6.imprint","IMPRINT",EDGE,{"derivedFrom":sQuery(id+"F6.wireOp",EDGE,"E37.5.0.2")}),-1.0]])]});
            var Q25;
            Q25=makeQuery(id+"F6.imprint","IMPRINT",FACE,{"disambiguationData":[TD([[makeQuery(id+"F6.imprint","IMPRINT",EDGE,{"derivedFrom":sQuery(id+"F6.wireOp",EDGE,"E37.5.0.10")}),-1.0]])]});
            var Q26;
            Q26=makeQuery(id+"F6.imprint","IMPRINT",FACE,{"disambiguationData":[TD([[makeQuery(id+"F6.imprint","IMPRINT",EDGE,{"derivedFrom":sQuery(id+"F6.wireOp",EDGE,"E37.6.0.6")}),1.0]])]});
            var Q27;
            {var subQ0=sQuery(id+"F6.wireOp",EDGE,"E37.6.0.0");Q27=makeQuery(id+"F6.imprint","IMPRINT",FACE,{"disambiguationData":[TD([[makeQuery(id+"F6.imprint","IMPRINT",EDGE,{"derivedFrom":subQ0}),1.0]])]});}
            var Q28;
            Q28=makeQuery(id+"F6.imprint","IMPRINT",FACE,{"disambiguationData":[TD([[makeQuery(id+"F6.imprint","IMPRINT",EDGE,{"derivedFrom":sQuery(id+"F6.wireOp",EDGE,"E37.6.0.2")}),-1.0]])]});
            var Q29;
            Q29=makeQuery(id+"F6.imprint","IMPRINT",FACE,{"disambiguationData":[TD([[makeQuery(id+"F6.imprint","IMPRINT",EDGE,{"derivedFrom":sQuery(id+"F6.wireOp",EDGE,"E37.6.0.10")}),-1.0]])]});
            var Q30;
            Q30=makeQuery(id+"F6.imprint","IMPRINT",FACE,{"disambiguationData":[TD([[makeQuery(id+"F6.imprint","IMPRINT",EDGE,{"derivedFrom":sQuery(id+"F6.wireOp",EDGE,"E37.7.0.6")}),1.0]])]});
            var Q31;
            {var subQ0=sQuery(id+"F6.wireOp",EDGE,"E37.7.0.0");Q31=makeQuery(id+"F6.imprint","IMPRINT",FACE,{"disambiguationData":[TD([[makeQuery(id+"F6.imprint","IMPRINT",EDGE,{"derivedFrom":subQ0}),1.0]])]});}
            var Q32;
            Q32=makeQuery(id+"F6.imprint","IMPRINT",FACE,{"disambiguationData":[TD([[makeQuery(id+"F6.imprint","IMPRINT",EDGE,{"derivedFrom":sQuery(id+"F6.wireOp",EDGE,"E37.7.0.2")}),-1.0]])]});
            var Q33;
            Q33=makeQuery(id+"F6.imprint","IMPRINT",FACE,{"disambiguationData":[TD([[makeQuery(id+"F6.imprint","IMPRINT",EDGE,{"derivedFrom":sQuery(id+"F6.wireOp",EDGE,"E37.8.0.6")}),1.0]])]});
            var Q34;
            Q34=makeQuery(id+"F6.imprint","IMPRINT",FACE,{"disambiguationData":[TD([[makeQuery(id+"F6.imprint","IMPRINT",EDGE,{"derivedFrom":sQuery(id+"F6.wireOp",EDGE,"E37.7.0.10")}),-1.0]])]});
            var Q35;
            {var subQ0=sQuery(id+"F6.wireOp",EDGE,"E37.8.0.0");Q35=makeQuery(id+"F6.imprint","IMPRINT",FACE,{"disambiguationData":[TD([[makeQuery(id+"F6.imprint","IMPRINT",EDGE,{"derivedFrom":subQ0}),1.0]])]});}
            var Q36;
            Q36=makeQuery(id+"F6.imprint","IMPRINT",FACE,{"disambiguationData":[TD([[makeQuery(id+"F6.imprint","IMPRINT",EDGE,{"derivedFrom":sQuery(id+"F6.wireOp",EDGE,"E37.8.0.2")}),-1.0]])]});
            var Q37;
            Q37=makeQuery(id+"F6.imprint","IMPRINT",FACE,{"disambiguationData":[TD([[makeQuery(id+"F6.imprint","IMPRINT",EDGE,{"derivedFrom":sQuery(id+"F6.wireOp",EDGE,"E37.9.0.6")}),1.0]])]});
            var Q38;
            Q38=makeQuery(id+"F6.imprint","IMPRINT",FACE,{"disambiguationData":[TD([[makeQuery(id+"F6.imprint","IMPRINT",EDGE,{"derivedFrom":sQuery(id+"F6.wireOp",EDGE,"E37.8.0.10")}),-1.0]])]});
            var Q39;
            Q39=makeQuery(id+"F6.imprint","IMPRINT",FACE,{"disambiguationData":[TD([[makeQuery(id+"F6.imprint","IMPRINT",EDGE,{"derivedFrom":sQuery(id+"F6.wireOp",EDGE,"E37.9.0.10")}),-1.0]])]});
            var Q40;
            {var subQ0=sQuery(id+"F6.wireOp",EDGE,"E37.9.0.0");Q40=makeQuery(id+"F6.imprint","IMPRINT",FACE,{"disambiguationData":[TD([[makeQuery(id+"F6.imprint","IMPRINT",EDGE,{"derivedFrom":subQ0}),1.0]])]});}
            var Q41;
            Q41=makeQuery(id+"F6.imprint","IMPRINT",FACE,{"disambiguationData":[TD([[makeQuery(id+"F6.imprint","IMPRINT",EDGE,{"derivedFrom":sQuery(id+"F6.wireOp",EDGE,"E37.9.0.2")}),-1.0]])]});
            var Q42;
            Q42=makeQuery(id+"F6.imprint","IMPRINT",FACE,{"disambiguationData":[TD([[makeQuery(id+"F6.imprint","IMPRINT",EDGE,{"derivedFrom":sQuery(id+"F6.wireOp",EDGE,"E37.10.0.6")}),1.0]])]});
            var Q43;
            Q43=makeQuery(id+"F6.imprint","IMPRINT",FACE,{"disambiguationData":[TD([[makeQuery(id+"F6.imprint","IMPRINT",EDGE,{"derivedFrom":sQuery(id+"F6.wireOp",EDGE,"E37.10.0.10")}),-1.0]])]});
            var Q44;
            Q44=makeQuery(id+"F6.imprint","IMPRINT",FACE,{"disambiguationData":[TD([[makeQuery(id+"F6.imprint","IMPRINT",EDGE,{"derivedFrom":sQuery(id+"F6.wireOp",EDGE,"E37.11.0.10")}),-1.0]])]});
            var Q45;
            Q45=makeQuery(id+"F6.imprint","IMPRINT",FACE,{"disambiguationData":[TD([[makeQuery(id+"F6.imprint","IMPRINT",EDGE,{"derivedFrom":sQuery(id+"F6.wireOp",EDGE,"E37.11.0.6")}),1.0]])]});
            var Q46;
            Q46=makeQuery(id+"F6.imprint","IMPRINT",FACE,{"disambiguationData":[TD([[makeQuery(id+"F6.imprint","IMPRINT",EDGE,{"derivedFrom":sQuery(id+"F6.wireOp",EDGE,"E37.10.0.2")}),-1.0]])]});
            var Q47;
            {var subQ0=sQuery(id+"F6.wireOp",EDGE,"E37.10.0.1");Q47=makeQuery(id+"F6.imprint","IMPRINT",FACE,{"disambiguationData":[TD([[makeQuery(id+"F6.imprint","IMPRINT",EDGE,{"derivedFrom":subQ0}),1.0]])]});}
            var Q48;
            {var subQ0=sQuery(id+"F6.wireOp",EDGE,"E37.11.0.0");Q48=makeQuery(id+"F6.imprint","IMPRINT",FACE,{"disambiguationData":[TD([[makeQuery(id+"F6.imprint","IMPRINT",EDGE,{"derivedFrom":subQ0}),1.0]])]});}
            var Q49;
            {var subQ0=sQuery(id+"F6.wireOp",EDGE,"E37.11.0.2");Q49=makeQuery(id+"F6.imprint","IMPRINT",FACE,{"disambiguationData":[TD([[makeQuery(id+"F6.imprint","IMPRINT",EDGE,{"derivedFrom":subQ0}),-1.0]])]});}
            extrude(context, id + "F7", {"entities" : qUnion([Q0, Q1, Q2, Q3, Q4, Q5, Q6, Q7, Q8, Q9, Q10, Q11, Q12, Q13, Q14, Q15, Q16, Q17, Q18, Q19, Q20, Q21, Q22, Q23, Q24, Q25, Q26, Q27, Q28, Q29, Q30, Q31, Q32, Q33, Q34, Q35, Q36, Q37, Q38, Q39, Q40, Q41, Q42, Q43, Q44, Q45, Q46, Q47, Q48, Q49]), "operationType" : NewBodyOperationType.REMOVE, "endBound" : BoundingType.THROUGH_ALL, "oppositeDirection" : true, "depth" : 25 * mm, "offsetDistance" : 25 * mm});
        }
        {
            var Q0;
            {var subQ0=sQuery(id+"F6.wireOp",EDGE,"E11.0.2");Q0=makeQuery(id+"F7.boolean.opBoolean","MERGE",FACE,{"derivedFrom":[makeQuery(id+"F1.opExtrude","CAP_FACE",FACE,{"disambiguationData":[OSD([sQuery(id+"F0.wireOp",EDGE,"E0.bottom"),sQuery(id+"F0.wireOp",EDGE,"E0.top"),sQuery(id+"F0.wireOp",EDGE,"E0.left"),sQuery(id+"F0.wireOp",EDGE,"E0.right")])],"isStart":false})],"fromTools":[makeQuery(id+"F7.opExtrude","SWEPT_FACE",FACE,{"disambiguationData":[OSD([subQ0]),TDD([makeQuery(id+"F6.imprint","IMPRINT",EDGE,{"disambiguationData":[TD([[makeQuery(id+"F6.imprint","INTERSECT",VERTEX,{"derivedFrom":[subQ0,sQuery(id+"F6.wireOp",EDGE,"E37.11.0.12")]}),-1.0]])],"derivedFrom":subQ0})])]}),makeQuery(id+"F7.opExtrude","SWEPT_FACE",FACE,{"disambiguationData":[OSD([subQ0]),TDD([makeQuery(id+"F6.imprint","IMPRINT",EDGE,{"disambiguationData":[TD([[makeQuery(id+"F6.imprint","INTERSECT",VERTEX,{"derivedFrom":[subQ0,sQuery(id+"F6.wireOp",EDGE,"E37.10.0.12")]}),-1.0]])],"derivedFrom":subQ0})])]}),makeQuery(id+"F7.opExtrude","SWEPT_FACE",FACE,{"disambiguationData":[OSD([subQ0]),TDD([makeQuery(id+"F6.imprint","IMPRINT",EDGE,{"disambiguationData":[TD([[makeQuery(id+"F6.imprint","INTERSECT",VERTEX,{"derivedFrom":[subQ0,sQuery(id+"F6.wireOp",EDGE,"E37.9.0.12")]}),-1.0]])],"derivedFrom":subQ0})])]}),makeQuery(id+"F7.opExtrude","SWEPT_FACE",FACE,{"disambiguationData":[OSD([subQ0]),TDD([makeQuery(id+"F6.imprint","IMPRINT",EDGE,{"disambiguationData":[TD([[makeQuery(id+"F6.imprint","INTERSECT",VERTEX,{"derivedFrom":[subQ0,sQuery(id+"F6.wireOp",EDGE,"E37.8.0.12")]}),-1.0]])],"derivedFrom":subQ0})])]}),makeQuery(id+"F7.opExtrude","SWEPT_FACE",FACE,{"disambiguationData":[OSD([subQ0]),TDD([makeQuery(id+"F6.imprint","IMPRINT",EDGE,{"disambiguationData":[TD([[makeQuery(id+"F6.imprint","INTERSECT",VERTEX,{"derivedFrom":[subQ0,sQuery(id+"F6.wireOp",EDGE,"E37.7.0.12")]}),-1.0]])],"derivedFrom":subQ0})])]}),makeQuery(id+"F7.opExtrude","SWEPT_FACE",FACE,{"disambiguationData":[OSD([subQ0]),TDD([makeQuery(id+"F6.imprint","IMPRINT",EDGE,{"disambiguationData":[TD([[makeQuery(id+"F6.imprint","INTERSECT",VERTEX,{"derivedFrom":[subQ0,sQuery(id+"F6.wireOp",EDGE,"E37.6.0.12")]}),-1.0]])],"derivedFrom":subQ0})])]}),makeQuery(id+"F7.opExtrude","SWEPT_FACE",FACE,{"disambiguationData":[OSD([subQ0]),TDD([makeQuery(id+"F6.imprint","IMPRINT",EDGE,{"disambiguationData":[TD([[makeQuery(id+"F6.imprint","INTERSECT",VERTEX,{"derivedFrom":[subQ0,sQuery(id+"F6.wireOp",EDGE,"E37.5.0.12")]}),-1.0]])],"derivedFrom":subQ0})])]}),makeQuery(id+"F7.opExtrude","SWEPT_FACE",FACE,{"disambiguationData":[OSD([subQ0]),TDD([makeQuery(id+"F6.imprint","IMPRINT",EDGE,{"disambiguationData":[TD([[makeQuery(id+"F6.imprint","INTERSECT",VERTEX,{"derivedFrom":[subQ0,sQuery(id+"F6.wireOp",EDGE,"E37.4.0.12")]}),-1.0]])],"derivedFrom":subQ0})])]}),makeQuery(id+"F7.opExtrude","SWEPT_FACE",FACE,{"disambiguationData":[OSD([subQ0]),TDD([makeQuery(id+"F6.imprint","IMPRINT",EDGE,{"disambiguationData":[TD([[makeQuery(id+"F6.imprint","INTERSECT",VERTEX,{"derivedFrom":[subQ0,sQuery(id+"F6.wireOp",EDGE,"E37.3.0.12")]}),-1.0]])],"derivedFrom":subQ0})])]}),makeQuery(id+"F7.opExtrude","SWEPT_FACE",FACE,{"disambiguationData":[OSD([subQ0]),TDD([makeQuery(id+"F6.imprint","IMPRINT",EDGE,{"disambiguationData":[TD([[makeQuery(id+"F6.imprint","INTERSECT",VERTEX,{"derivedFrom":[subQ0,sQuery(id+"F6.wireOp",EDGE,"E37.2.0.12")]}),-1.0]])],"derivedFrom":subQ0})])]}),makeQuery(id+"F7.opExtrude","SWEPT_FACE",FACE,{"disambiguationData":[OSD([subQ0]),TDD([makeQuery(id+"F6.imprint","IMPRINT",EDGE,{"disambiguationData":[TD([[makeQuery(id+"F6.imprint","INTERSECT",VERTEX,{"derivedFrom":[subQ0,sQuery(id+"F6.wireOp",EDGE,"E37.1.0.12")]}),-1.0]])],"derivedFrom":subQ0})])]}),makeQuery(id+"F7.opExtrude","SWEPT_FACE",FACE,{"disambiguationData":[OSD([subQ0]),TDD([makeQuery(id+"F6.imprint","IMPRINT",EDGE,{"disambiguationData":[TD([[makeQuery(id+"F6.imprint","INTERSECT",VERTEX,{"derivedFrom":[subQ0,sQuery(id+"F6.wireOp",EDGE,"E32.MirrorCS")]}),1.0]])],"derivedFrom":subQ0})])]}),makeQuery(id+"F7.opExtrude","SWEPT_FACE",FACE,{"disambiguationData":[OSD([subQ0]),TDD([makeQuery(id+"F6.imprint","IMPRINT",EDGE,{"disambiguationData":[TD([[makeQuery(id+"F6.imprint","INTERSECT",VERTEX,{"derivedFrom":[sQuery(id+"F6.wireOp",EDGE,"E10.0.3"),subQ0]}),1.0]])],"derivedFrom":subQ0})])]})]});}
            var sketch = newSketch(context, id + "F8", { "sketchPlane" : qUnion([Q0])});
            skLineSegment(sketch, "E43.0.0", {"start": v(0, 3.5) * mm, "end": v(50, 3.5) * mm});
            skLineSegment(sketch, "E43.0.1", {"start": v(50, 3.5) * mm, "end": v(50, 4.74) * mm});
            skLineSegment(sketch, "E43.0.2", {"start": v(50, 4.74) * mm, "end": v(46.5, 4.74) * mm});
            skLineSegment(sketch, "E43.0.3", {"start": v(46.5, 4.74) * mm, "end": v(46.5, 13.26) * mm});
            skLineSegment(sketch, "E43.0.4", {"start": v(46.5, 13.26) * mm, "end": v(50, 13.26) * mm});
            skLineSegment(sketch, "E43.0.5", {"start": v(50, 13.26) * mm, "end": v(50, 19.99) * mm});
            skLineSegment(sketch, "E43.0.6", {"start": v(50, 19.99) * mm, "end": v(46.5, 19.99) * mm});
            skLineSegment(sketch, "E43.0.7", {"start": v(46.5, 19.99) * mm, "end": v(46.5, 28.5) * mm});
            skLineSegment(sketch, "E43.0.8", {"start": v(46.5, 28.5) * mm, "end": v(50, 28.5) * mm});
            skLineSegment(sketch, "E43.0.9", {"start": v(50, 28.5) * mm, "end": v(50, 35.23) * mm});
            skLineSegment(sketch, "E43.0.10", {"start": v(50, 35.23) * mm, "end": v(46.5, 35.23) * mm});
            skLineSegment(sketch, "E43.0.11", {"start": v(46.5, 35.23) * mm, "end": v(46.5, 43.74) * mm});
            skLineSegment(sketch, "E43.0.12", {"start": v(46.5, 43.74) * mm, "end": v(50, 43.74) * mm});
            skLineSegment(sketch, "E43.0.13", {"start": v(50, 43.74) * mm, "end": v(50, 50.47) * mm});
            skLineSegment(sketch, "E43.0.14", {"start": v(50, 50.47) * mm, "end": v(46.5, 50.47) * mm});
            skLineSegment(sketch, "E43.0.15", {"start": v(46.5, 50.47) * mm, "end": v(46.5, 58.99) * mm});
            skLineSegment(sketch, "E43.0.16", {"start": v(46.5, 58.99) * mm, "end": v(50, 58.99) * mm});
            skLineSegment(sketch, "E43.0.17", {"start": v(50, 58.99) * mm, "end": v(50, 65.71) * mm});
            skLineSegment(sketch, "E43.0.18", {"start": v(50, 65.71) * mm, "end": v(46.5, 65.71) * mm});
            skLineSegment(sketch, "E43.0.19", {"start": v(46.5, 65.71) * mm, "end": v(46.5, 74.23) * mm});
            skLineSegment(sketch, "E43.0.20", {"start": v(46.5, 74.23) * mm, "end": v(50, 74.23) * mm});
            skLineSegment(sketch, "E43.0.21", {"start": v(50, 74.23) * mm, "end": v(50, 80.96) * mm});
            skLineSegment(sketch, "E43.0.22", {"start": v(50, 80.96) * mm, "end": v(46.5, 80.96) * mm});
            skLineSegment(sketch, "E43.0.23", {"start": v(46.5, 80.96) * mm, "end": v(46.5, 89.47) * mm});
            skLineSegment(sketch, "E43.0.24", {"start": v(46.5, 89.47) * mm, "end": v(50, 89.47) * mm});
            skLineSegment(sketch, "E43.0.25", {"start": v(50, 89.47) * mm, "end": v(50, 96.2) * mm});
            skLineSegment(sketch, "E43.0.26", {"start": v(50, 96.2) * mm, "end": v(46.5, 96.2) * mm});
            skLineSegment(sketch, "E43.0.27", {"start": v(46.5, 96.2) * mm, "end": v(46.5, 104.72) * mm});
            skLineSegment(sketch, "E43.0.28", {"start": v(46.5, 104.72) * mm, "end": v(50, 104.72) * mm});
            skLineSegment(sketch, "E43.0.29", {"start": v(50, 104.72) * mm, "end": v(50, 111.44) * mm});
            skLineSegment(sketch, "E43.0.30", {"start": v(50, 111.44) * mm, "end": v(46.5, 111.44) * mm});
            skLineSegment(sketch, "E43.0.31", {"start": v(46.5, 111.44) * mm, "end": v(46.5, 119.96) * mm});
            skLineSegment(sketch, "E43.0.32", {"start": v(46.5, 119.96) * mm, "end": v(50, 119.96) * mm});
            skLineSegment(sketch, "E43.0.33", {"start": v(50, 119.96) * mm, "end": v(50, 126.69) * mm});
            skLineSegment(sketch, "E43.0.34", {"start": v(50, 126.69) * mm, "end": v(46.5, 126.69) * mm});
            skLineSegment(sketch, "E43.0.35", {"start": v(46.5, 126.69) * mm, "end": v(46.5, 135.2) * mm});
            skLineSegment(sketch, "E43.0.36", {"start": v(46.5, 135.2) * mm, "end": v(50, 135.2) * mm});
            skLineSegment(sketch, "E43.0.37", {"start": v(50, 135.2) * mm, "end": v(50, 141.93) * mm});
            skLineSegment(sketch, "E43.0.38", {"start": v(50, 141.93) * mm, "end": v(46.5, 141.93) * mm});
            skLineSegment(sketch, "E43.0.39", {"start": v(46.5, 141.93) * mm, "end": v(46.5, 150.44) * mm});
            skLineSegment(sketch, "E43.0.40", {"start": v(46.5, 150.44) * mm, "end": v(50, 150.44) * mm});
            skLineSegment(sketch, "E43.0.41", {"start": v(50, 150.44) * mm, "end": v(50, 157.17) * mm});
            skLineSegment(sketch, "E43.0.42", {"start": v(50, 157.17) * mm, "end": v(46.5, 157.17) * mm});
            skLineSegment(sketch, "E43.0.43", {"start": v(46.5, 157.17) * mm, "end": v(46.5, 165.69) * mm});
            skLineSegment(sketch, "E43.0.44", {"start": v(46.5, 165.69) * mm, "end": v(50, 165.69) * mm});
            skLineSegment(sketch, "E43.0.45", {"start": v(50, 165.69) * mm, "end": v(50, 172.42) * mm});
            skLineSegment(sketch, "E43.0.46", {"start": v(50, 172.42) * mm, "end": v(46.5, 172.42) * mm});
            skLineSegment(sketch, "E43.0.47", {"start": v(46.5, 172.42) * mm, "end": v(46.5, 180.93) * mm});
            skLineSegment(sketch, "E43.0.48", {"start": v(46.5, 180.93) * mm, "end": v(50, 180.93) * mm});
            skLineSegment(sketch, "E43.0.49", {"start": v(50, 180.93) * mm, "end": v(50, 187.66) * mm});
            skLineSegment(sketch, "E43.0.50", {"start": v(50, 187.66) * mm, "end": v(46.5, 187.66) * mm});
            skLineSegment(sketch, "E43.0.51", {"start": v(46.5, 187.66) * mm, "end": v(46.5, 194.88) * mm});
            skLineSegment(sketch, "E43.0.52", {"start": v(46.5, 194.88) * mm, "end": v(3.5, 194.88) * mm});
            skLineSegment(sketch, "E43.0.53", {"start": v(3.5, 194.88) * mm, "end": v(3.5, 187.66) * mm});
            skLineSegment(sketch, "E43.0.54", {"start": v(3.5, 187.66) * mm, "end": v(0, 187.66) * mm});
            skLineSegment(sketch, "E43.0.55", {"start": v(0, 187.66) * mm, "end": v(0, 180.93) * mm});
            skLineSegment(sketch, "E43.0.56", {"start": v(0, 180.93) * mm, "end": v(3.5, 180.93) * mm});
            skLineSegment(sketch, "E43.0.57", {"start": v(3.5, 180.93) * mm, "end": v(3.5, 172.42) * mm});
            skLineSegment(sketch, "E43.0.58", {"start": v(3.5, 172.42) * mm, "end": v(0, 172.42) * mm});
            skLineSegment(sketch, "E43.0.59", {"start": v(0, 172.42) * mm, "end": v(0, 165.69) * mm});
            skLineSegment(sketch, "E43.0.60", {"start": v(0, 165.69) * mm, "end": v(3.5, 165.69) * mm});
            skLineSegment(sketch, "E43.0.61", {"start": v(3.5, 165.69) * mm, "end": v(3.5, 157.17) * mm});
            skLineSegment(sketch, "E43.0.62", {"start": v(3.5, 157.17) * mm, "end": v(0, 157.17) * mm});
            skLineSegment(sketch, "E43.0.63", {"start": v(0, 157.17) * mm, "end": v(0, 150.44) * mm});
            skLineSegment(sketch, "E43.0.64", {"start": v(0, 150.44) * mm, "end": v(3.5, 150.44) * mm});
            skLineSegment(sketch, "E43.0.65", {"start": v(3.5, 150.44) * mm, "end": v(3.5, 141.93) * mm});
            skLineSegment(sketch, "E43.0.66", {"start": v(3.5, 141.93) * mm, "end": v(0, 141.93) * mm});
            skLineSegment(sketch, "E43.0.67", {"start": v(0, 141.93) * mm, "end": v(0, 135.2) * mm});
            skLineSegment(sketch, "E43.0.68", {"start": v(0, 135.2) * mm, "end": v(3.5, 135.2) * mm});
            skLineSegment(sketch, "E43.0.69", {"start": v(3.5, 135.2) * mm, "end": v(3.5, 126.69) * mm});
            skLineSegment(sketch, "E43.0.70", {"start": v(3.5, 126.69) * mm, "end": v(0, 126.69) * mm});
            skLineSegment(sketch, "E43.0.71", {"start": v(0, 126.69) * mm, "end": v(0, 119.96) * mm});
            skLineSegment(sketch, "E43.0.72", {"start": v(0, 119.96) * mm, "end": v(3.5, 119.96) * mm});
            skLineSegment(sketch, "E43.0.73", {"start": v(3.5, 119.96) * mm, "end": v(3.5, 111.44) * mm});
            skLineSegment(sketch, "E43.0.74", {"start": v(3.5, 111.44) * mm, "end": v(0, 111.44) * mm});
            skLineSegment(sketch, "E43.0.75", {"start": v(0, 111.44) * mm, "end": v(0, 104.72) * mm});
            skLineSegment(sketch, "E43.0.76", {"start": v(0, 104.72) * mm, "end": v(3.5, 104.72) * mm});
            skLineSegment(sketch, "E43.0.77", {"start": v(3.5, 104.72) * mm, "end": v(3.5, 96.2) * mm});
            skLineSegment(sketch, "E43.0.78", {"start": v(3.5, 96.2) * mm, "end": v(0, 96.2) * mm});
            skLineSegment(sketch, "E43.0.79", {"start": v(0, 96.2) * mm, "end": v(0, 89.47) * mm});
            skLineSegment(sketch, "E43.0.80", {"start": v(0, 89.47) * mm, "end": v(3.5, 89.47) * mm});
            skLineSegment(sketch, "E43.0.81", {"start": v(3.5, 89.47) * mm, "end": v(3.5, 80.96) * mm});
            skLineSegment(sketch, "E43.0.82", {"start": v(3.5, 80.96) * mm, "end": v(0, 80.96) * mm});
            skLineSegment(sketch, "E43.0.83", {"start": v(0, 80.96) * mm, "end": v(0, 74.23) * mm});
            skLineSegment(sketch, "E43.0.84", {"start": v(0, 74.23) * mm, "end": v(3.5, 74.23) * mm});
            skLineSegment(sketch, "E43.0.85", {"start": v(3.5, 74.23) * mm, "end": v(3.5, 65.71) * mm});
            skLineSegment(sketch, "E43.0.86", {"start": v(3.5, 65.71) * mm, "end": v(0, 65.71) * mm});
            skLineSegment(sketch, "E43.0.87", {"start": v(0, 65.71) * mm, "end": v(0, 58.99) * mm});
            skLineSegment(sketch, "E43.0.88", {"start": v(0, 58.99) * mm, "end": v(3.5, 58.99) * mm});
            skLineSegment(sketch, "E43.0.89", {"start": v(3.5, 58.99) * mm, "end": v(3.5, 50.47) * mm});
            skLineSegment(sketch, "E43.0.90", {"start": v(3.5, 50.47) * mm, "end": v(0, 50.47) * mm});
            skLineSegment(sketch, "E43.0.91", {"start": v(0, 50.47) * mm, "end": v(0, 43.74) * mm});
            skLineSegment(sketch, "E43.0.92", {"start": v(0, 43.74) * mm, "end": v(3.5, 43.74) * mm});
            skLineSegment(sketch, "E43.0.93", {"start": v(3.5, 43.74) * mm, "end": v(3.5, 35.23) * mm});
            skLineSegment(sketch, "E43.0.94", {"start": v(3.5, 35.23) * mm, "end": v(0, 35.23) * mm});
            skLineSegment(sketch, "E43.0.95", {"start": v(0, 35.23) * mm, "end": v(0, 28.5) * mm});
            skLineSegment(sketch, "E43.0.96", {"start": v(0, 28.5) * mm, "end": v(3.5, 28.5) * mm});
            skLineSegment(sketch, "E43.0.97", {"start": v(3.5, 28.5) * mm, "end": v(3.5, 19.99) * mm});
            skLineSegment(sketch, "E43.0.98", {"start": v(3.5, 19.99) * mm, "end": v(0, 19.99) * mm});
            skLineSegment(sketch, "E43.0.99", {"start": v(0, 19.99) * mm, "end": v(0, 13.26) * mm});
            skLineSegment(sketch, "E43.0.100", {"start": v(0, 13.26) * mm, "end": v(3.5, 13.26) * mm});
            skLineSegment(sketch, "E43.0.101", {"start": v(3.5, 13.26) * mm, "end": v(3.5, 4.74) * mm});
            skLineSegment(sketch, "E43.0.102", {"start": v(3.5, 4.74) * mm, "end": v(0, 4.74) * mm});
            skLineSegment(sketch, "E43.0.103", {"start": v(0, 4.74) * mm, "end": v(0, 3.5) * mm});
            skLineSegment(sketch, "E44.0", {"start": v(3.5, 155) * mm, "end": v(3.5, 3.5) * mm});
            skLineSegment(sketch, "E45.0", {"start": v(46.5, 3.5) * mm, "end": v(46.5, 155) * mm});
            skLineSegment(sketch, "E46.0", {"start": v(3.5, 3.5) * mm, "end": v(46.5, 3.5) * mm});
            skPoint(sketch, "E47", {"position": v(9.75, 42) * mm});
            skPoint(sketch, "E48", {"position": v(40.25, 42) * mm});
            skPoint(sketch, "E49", {"position": v(9.75, 11.5) * mm});
            skPoint(sketch, "E50", {"position": v(40.25, 11.5) * mm});
            skLineSegment(sketch, "E51", {"start": v(9.75, 11.5) * mm, "end": v(40.25, 11.5) * mm, "construction": true});
            skLineSegment(sketch, "E52", {"start": v(25, 11.5) * mm, "end": v(25, 3.5) * mm, "construction": true});
            skSolve(sketch);
        }
        {
            var Q0;
            Q0=sQuery(id+"F8.wireOp",VERTEX,"E47");
            var Q1;
            Q1=sQuery(id+"F8.wireOp",VERTEX,"E48");
            var Q2;
            Q2=sQuery(id+"F8.wireOp",VERTEX,"E49");
            var Q3;
            Q3=sQuery(id+"F8.wireOp",VERTEX,"E50");
            var Q4;
            Q4=makeQuery(id+"F1.opExtrude","SWEPT_BODY",BODY,{"disambiguationData":[OSD([sQuery(id+"F0.wireOp",EDGE,"E0.bottom"),sQuery(id+"F0.wireOp",EDGE,"E0.top"),sQuery(id+"F0.wireOp",EDGE,"E0.left"),sQuery(id+"F0.wireOp",EDGE,"E0.right")])]});
            hole(context, id + "F9", {"style" : HoleStyle.SIMPLE, "endStyle" : HoleEndStyle.THROUGH, "standardTappedOrClearance" : lookupTablePath({ "fit" : "Close", "standard" : "ISO", "size" : "M3", "type" : "Clearance" }), "standardBlindInLast" : lookupTablePath({ "fit" : "Close", "standard" : "ISO", "size" : "M3", "type" : "Clearance" }), "holeDiameter" : 3.2 * mm, "majorDiameter" : 3 * mm, "isTappedThrough" : true, "tappedDepth" : 12 * mm, "tapClearance" : 3, "locations" : qUnion([Q0, Q1, Q2, Q3]), "scope" : qUnion([Q4])});
        }
    });
